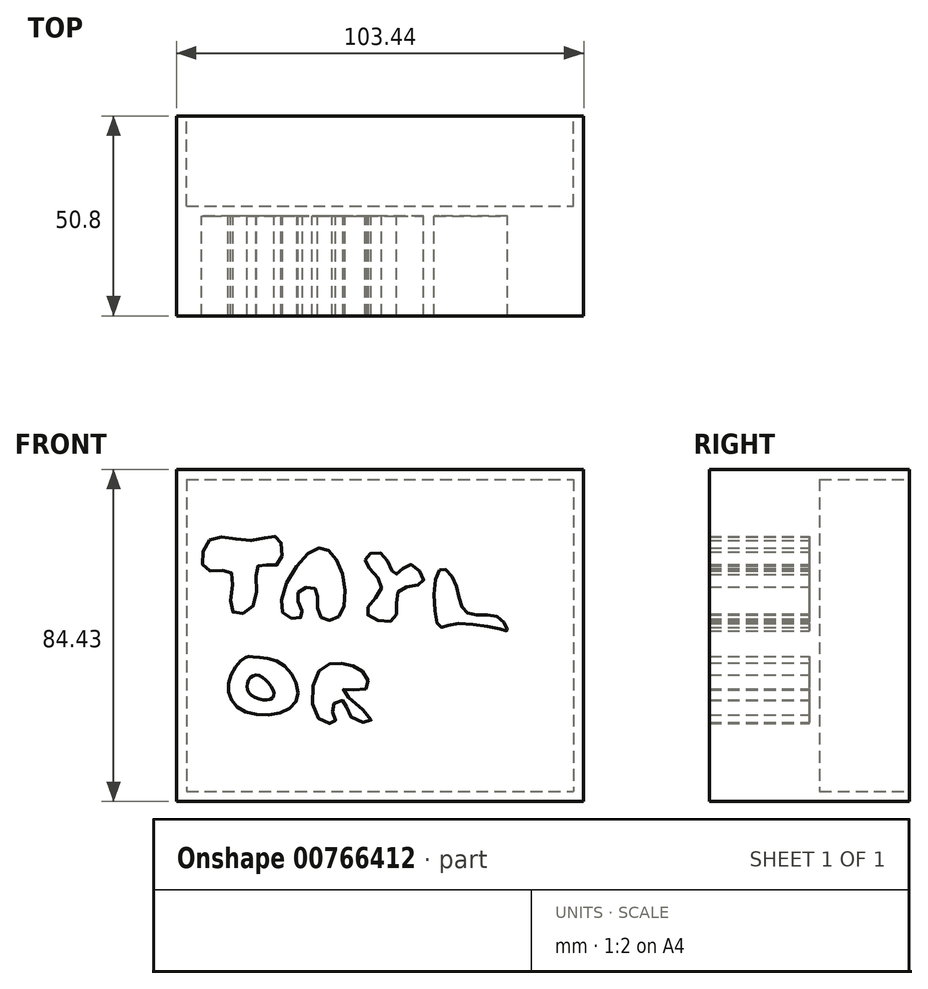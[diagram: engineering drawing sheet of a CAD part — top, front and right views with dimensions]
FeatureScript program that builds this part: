
annotation { "Feature Type Name" : "Feature", "Feature Type Description" : "" }
export const myFeature = defineFeature(function(context is Context, id is Id, definition is map)
    precondition{}
    {
        {
            var Q0;
            Q0=qCreatedBy(makeId("Front.planeOp"),FACE);
            var sketch = newSketch(context, id + "F0", { "sketchPlane" : qUnion([Q0])});
            skLineSegment(sketch, "E0.bottom", {"start": v(-97.84, 28.56) * mm, "end": v(5.6, 28.56) * mm});
            skLineSegment(sketch, "E0.top", {"start": v(-97.84, -55.87) * mm, "end": v(5.6, -55.87) * mm});
            skLineSegment(sketch, "E0.left", {"start": v(-97.84, 28.56) * mm, "end": v(-97.84, -55.87) * mm});
            skLineSegment(sketch, "E0.right", {"start": v(5.6, 28.56) * mm, "end": v(5.6, -55.87) * mm});
            skSolve(sketch);
        }
        {
            var Q0;
            Q0=makeQuery(id+"F0.imprint","IMPRINT",FACE,{"disambiguationData":[TD([[makeQuery(id+"F0.imprint","IMPRINT",EDGE,{"derivedFrom":sQuery(id+"F0.wireOp",EDGE,"E0.bottom")}),-1.0]])]});
            extrude(context, id + "F1", {"entities" : qUnion([Q0]), "depth" : 25.4 * mm, "offsetDistance" : 25.4 * mm});
        }
        {
            var Q0;
            Q0=makeQuery(id+"F1.opExtrude","CAP_FACE",FACE,{"disambiguationData":[OSD([sQuery(id+"F0.wireOp",EDGE,"E0.bottom"),sQuery(id+"F0.wireOp",EDGE,"E0.top"),sQuery(id+"F0.wireOp",EDGE,"E0.left"),sQuery(id+"F0.wireOp",EDGE,"E0.right")])],"isStart":true});
            shell(context, id + "F2", {"entities" : qUnion([Q0]), "thickness" : 2.54 * mm});
        }
        {
            var Q0;
            Q0=makeQuery(id+"F1.opExtrude","CAP_FACE",FACE,{"disambiguationData":[OSD([sQuery(id+"F0.wireOp",EDGE,"E0.bottom"),sQuery(id+"F0.wireOp",EDGE,"E0.top"),sQuery(id+"F0.wireOp",EDGE,"E0.left"),sQuery(id+"F0.wireOp",EDGE,"E0.right")])],"isStart":false});
            var sketch = newSketch(context, id + "F3", { "sketchPlane" : qUnion([Q0])});
            skFitSpline(sketch, "E1", {"points": [v(-89.42, 10.6) * mm, v(-78.87, 10.46) * mm, v(-71.9, 11.05) * mm, v(-72.19, 4.37) * mm, v(-77.1, 4.07) * mm, v(-78.28, -6.03) * mm, v(-83.77, -7.37) * mm, v(-83.92, 2.29) * mm, v(-90.46, 3.18) * mm, v(-89.42, 10.6) * mm]});
            skFitSpline(sketch, "E2", {"points": [v(-70.85, -7.81) * mm, v(-65.95, -8.7) * mm, v(-67.14, -3.2) * mm, v(-62.68, -1.72) * mm, v(-61.5, -8.56) * mm, v(-56.44, -8.7) * mm, v(-57.19, 5.55) * mm, v(-63.57, 7.78) * mm, v(-70.85, -7.81) * mm]});
            skFitSpline(sketch, "E3", {"points": [v(-62.98, 2.43) * mm, v(-63.42, 0) * mm, v(-60.3, 0) * mm, v(-62.98, 2.43) * mm]});
            skFitSpline(sketch, "E4", {"points": [v(-49.9, 5.55) * mm, v(-45.75, -1.28) * mm, v(-49.61, -7.81) * mm, v(-42.63, -9.6) * mm, v(-41.44, -2.32) * mm, v(-35.2, 0) * mm, v(-38.62, 4.37) * mm, v(-42.33, 1.84) * mm, v(-45.75, 7.19) * mm, v(-49.9, 5.55) * mm]});
            skFitSpline(sketch, "E5", {"points": [v(-31.04, 3.03) * mm, v(-31.34, -11.08) * mm, v(-27.48, -10.79) * mm, v(-14.26, -12.42) * mm, v(-13.81, -12.42) * mm, v(-16.04, -9) * mm, v(-24.21, -7.81) * mm, v(-27.18, 0) * mm, v(-31.04, 3.03) * mm]});
            skFitSpline(sketch, "E6", {"points": [v(-80.36, -19.25) * mm, v(-84.52, -25.2) * mm, v(-80.95, -32.77) * mm, v(-67.73, -30.84) * mm, v(-70.85, -21.03) * mm, v(-78.58, -19.1) * mm, v(-80.36, -19.25) * mm]});
            skFitSpline(sketch, "E7", {"points": [v(-77.68, -23.7) * mm, v(-79.47, -28.16) * mm, v(-73.23, -29.2) * mm, v(-77.68, -23.7) * mm]});
            skFitSpline(sketch, "E8", {"points": [v(-61.64, -22.67) * mm, v(-61.64, -34.85) * mm, v(-57.48, -35.44) * mm, v(-58.37, -31.88) * mm, v(-55.4, -30.24) * mm, v(-53.47, -34.4) * mm, v(-48.42, -35.15) * mm, v(-55.55, -27.57) * mm, v(-49.9, -27.27) * mm, v(-49.9, -23.56) * mm, v(-54.96, -20.89) * mm, v(-61.64, -22.67) * mm]});
            skFitSpline(sketch, "E9", {"points": [v(-57.63, -24.6) * mm, v(-54.51, -24.15) * mm, v(-55.55, -25.79) * mm, v(-57.63, -24.6) * mm]});
            skSolve(sketch);
        }
        {
            var Q0;
            Q0=makeQuery(id+"F3.imprint","IMPRINT",FACE,{"disambiguationData":[TD([[makeQuery(id+"F3.imprint","IMPRINT",EDGE,{"derivedFrom":sQuery(id+"F3.wireOp",EDGE,"E1")}),1.0]])]});
            var Q1;
            Q1=makeQuery(id+"F3.imprint","IMPRINT",FACE,{"disambiguationData":[TD([[makeQuery(id+"F3.imprint","IMPRINT",EDGE,{"derivedFrom":sQuery(id+"F3.wireOp",EDGE,"E7")}),1.0]])]});
            extrude(context, id + "F4", {"entities" : qUnion([Q0, Q1]), "operationType" : NewBodyOperationType.ADD, "depth" : 25.4 * mm, "offsetDistance" : 25.4 * mm});
        }
    });
